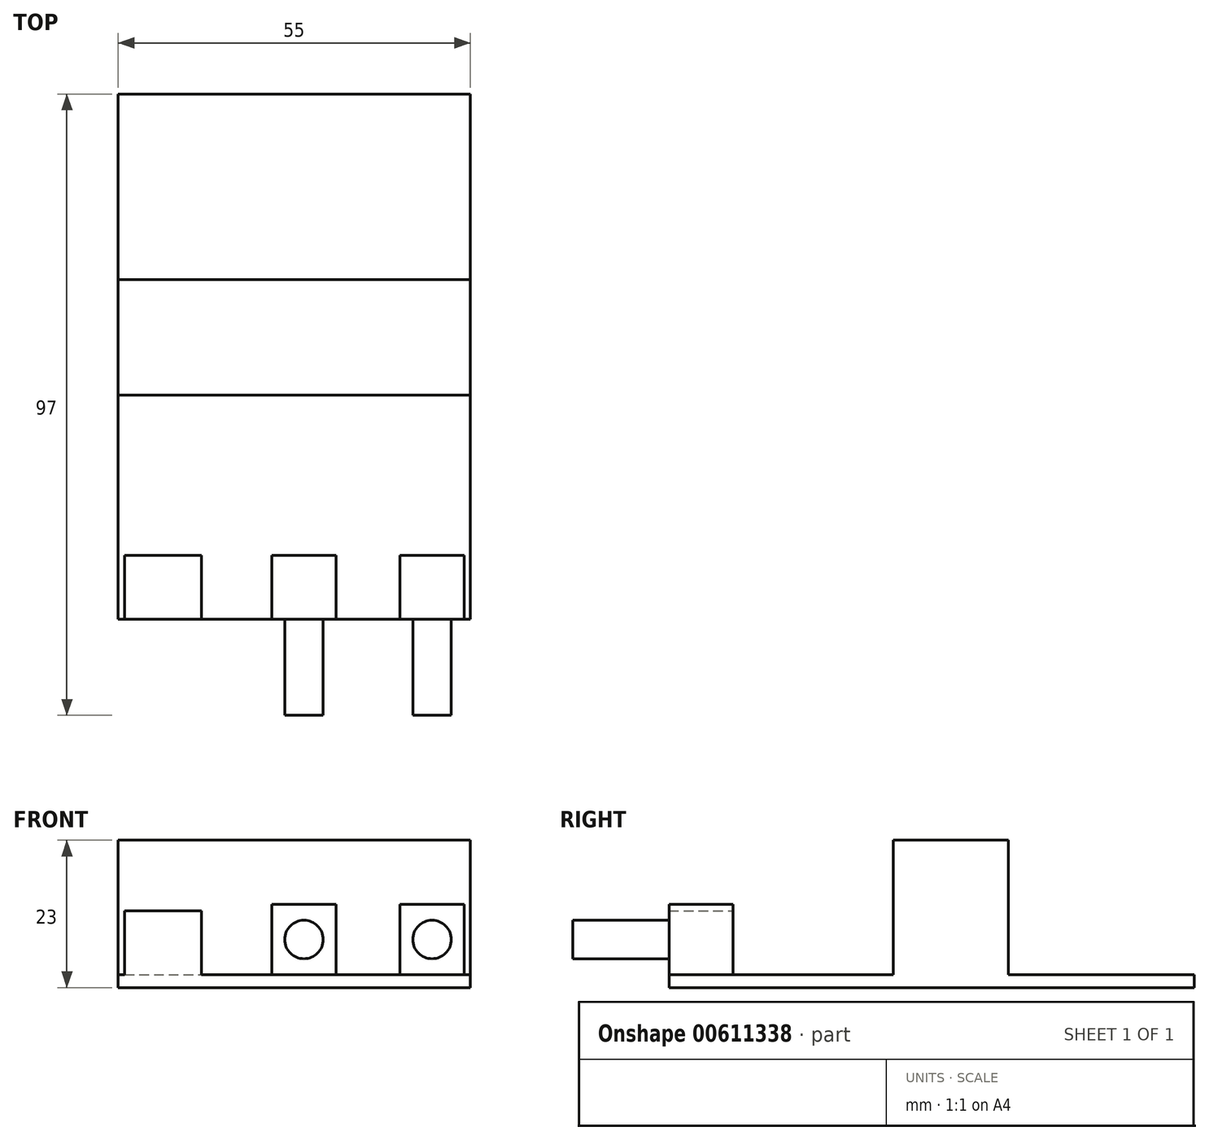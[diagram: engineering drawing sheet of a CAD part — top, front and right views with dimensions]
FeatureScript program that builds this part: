
annotation { "Feature Type Name" : "Feature", "Feature Type Description" : "" }
export const myFeature = defineFeature(function(context is Context, id is Id, definition is map)
    precondition{}
    {
        {
            var Q0;
            Q0=qCreatedBy(makeId("Top.planeOp"),FACE);
            var sketch = newSketch(context, id + "F0", { "sketchPlane" : qUnion([Q0])});
            skLineSegment(sketch, "E0.bottom", {"start": v(0, 0) * mm, "end": v(55, 0) * mm});
            skLineSegment(sketch, "E0.top", {"start": v(0, 82) * mm, "end": v(55, 82) * mm});
            skLineSegment(sketch, "E0.left", {"start": v(0, 0) * mm, "end": v(0, 82) * mm});
            skLineSegment(sketch, "E0.right", {"start": v(55, 0) * mm, "end": v(55, 82) * mm});
            skLineSegment(sketch, "E1.0", {"start": v(1, 10) * mm, "end": v(13, 10) * mm});
            skLineSegment(sketch, "E2.0", {"start": v(54, 0) * mm, "end": v(54, 10) * mm});
            skLineSegment(sketch, "E3.0", {"start": v(44, 0) * mm, "end": v(44, 10) * mm});
            skLineSegment(sketch, "E4.0", {"start": v(34, 0) * mm, "end": v(34, 10) * mm});
            skLineSegment(sketch, "E5.0", {"start": v(24, 0) * mm, "end": v(24, 10) * mm});
            skLineSegment(sketch, "E6.0", {"start": v(1, 0) * mm, "end": v(1, 10) * mm});
            skLineSegment(sketch, "E7.0", {"start": v(13, 0) * mm, "end": v(13, 10) * mm});
            skLineSegment(sketch, "E8.trimOffspring", {"start": v(24, 10) * mm, "end": v(34, 10) * mm});
            skLineSegment(sketch, "E9.trimOffspring", {"start": v(44, 10) * mm, "end": v(54, 10) * mm});
            skLineSegment(sketch, "E10.0", {"start": v(0, 35) * mm, "end": v(55, 35) * mm});
            skLineSegment(sketch, "E11.0", {"start": v(0, 53) * mm, "end": v(55, 53) * mm});
            skSolve(sketch);
        }
        {
            var Q0;
            Q0 = qSketchRegion(id + "F0", true);
            extrude(context, id + "F1", {"entities" : qUnion([Q0]), "oppositeDirection" : true, "depth" : 2 * mm, "offsetDistance" : 25 * mm});
        }
        {
            var Q0;
            {var subQ0=sQuery(id+"F0.wireOp",EDGE,"E4.0");Q0=makeQuery(id+"F0.imprint","IMPRINT",FACE,{"disambiguationData":[TD([[makeQuery(id+"F0.imprint","IMPRINT",EDGE,{"derivedFrom":subQ0}),1.0]])]});}
            var Q1;
            {var subQ0=sQuery(id+"F0.wireOp",EDGE,"E2.0");Q1=makeQuery(id+"F0.imprint","IMPRINT",FACE,{"disambiguationData":[TD([[makeQuery(id+"F0.imprint","IMPRINT",EDGE,{"derivedFrom":subQ0}),1.0]])]});}
            extrude(context, id + "F2", {"entities" : qUnion([Q0, Q1]), "depth" : 11 * mm, "offsetDistance" : 25 * mm});
        }
        {
            var Q0;
            Q0=makeQuery(id+"F0.imprint","IMPRINT",FACE,{"disambiguationData":[TD([[makeQuery(id+"F0.imprint","IMPRINT",EDGE,{"derivedFrom":sQuery(id+"F0.wireOp",EDGE,"E1.0")}),-1.0]])]});
            extrude(context, id + "F3", {"entities" : qUnion([Q0]), "operationType" : NewBodyOperationType.ADD, "depth" : 10 * mm, "offsetDistance" : 25 * mm});
        }
        {
            var Q0;
            {var subQ0=sQuery(id+"F0.wireOp",EDGE,"E10.0");Q0=makeQuery(id+"F0.imprint","IMPRINT",FACE,{"disambiguationData":[TD([[makeQuery(id+"F0.imprint","IMPRINT",EDGE,{"derivedFrom":subQ0}),1.0]])]});}
            extrude(context, id + "F4", {"entities" : qUnion([Q0]), "operationType" : NewBodyOperationType.ADD, "depth" : 21 * mm, "offsetDistance" : 25 * mm});
        }
        {
            var Q0;
            {var subQ0=sQuery(id+"F0.wireOp",EDGE,"E0.bottom");Q0=makeQuery(id+"F2.opExtrude","SWEPT_FACE",FACE,{"disambiguationData":[OSD([subQ0]),TDD([makeQuery(id+"F0.imprint","IMPRINT",EDGE,{"disambiguationData":[TD([[makeQuery(id+"F0.imprint","INTERSECT",VERTEX,{"derivedFrom":[subQ0,sQuery(id+"F0.wireOp",EDGE,"E4.0")]}),1.0]])],"derivedFrom":subQ0})])]});}
            var sketch = newSketch(context, id + "F5", { "sketchPlane" : qUnion([Q0])});
            skLineSegment(sketch, "E12", {"start": v(24, 11) * mm, "end": v(34, 0) * mm});
            skCircle(sketch, "E13", {"center": v(29, 5.5) * mm, "radius": 3 * mm});
            skCircle(sketch, "E14.1.0.0", {"center": v(49, 5.5) * mm, "radius": 3 * mm});
            skLineSegment(sketch, "E14.direction1", {"start": v(29, 5.5) * mm, "end": v(49, 5.5) * mm, "construction": true});
            skSolve(sketch);
        }
        {
            var Q0;
            Q0 = qSketchRegion(id + "F5", true);
            extrude(context, id + "F6", {"entities" : qUnion([Q0]), "depth" : 15 * mm, "offsetDistance" : 25 * mm});
        }
    });
